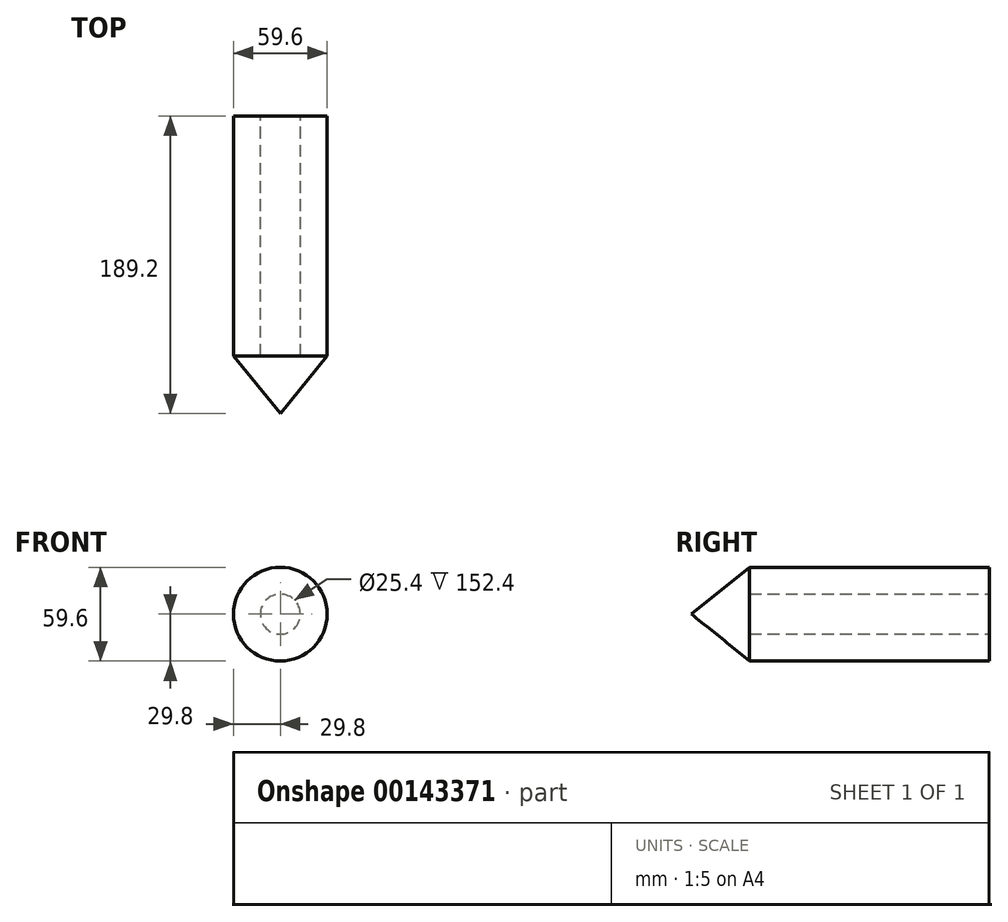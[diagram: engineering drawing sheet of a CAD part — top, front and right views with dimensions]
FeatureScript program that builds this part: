
annotation { "Feature Type Name" : "Feature", "Feature Type Description" : "" }
export const myFeature = defineFeature(function(context is Context, id is Id, definition is map)
    precondition{}
    {
        {
            var Q0;
            Q0=qCreatedBy(makeId("Front.planeOp"),FACE);
            var sketch = newSketch(context, id + "F0", { "sketchPlane" : qUnion([Q0])});
            skCircle(sketch, "E0", {"center": v(0, 0) * mm, "radius": 12.7 * mm});
            skCircle(sketch, "E1", {"center": v(0, 0) * mm, "radius": 29.8 * mm});
            skSolve(sketch);
        }
        {
            var Q0;
            Q0=makeQuery(id+"F0.imprint","IMPRINT",FACE,{"disambiguationData":[TD([[makeQuery(id+"F0.imprint","IMPRINT",EDGE,{"derivedFrom":sQuery(id+"F0.wireOp",EDGE,"E0")}),-1.0]])]});
            extrude(context, id + "F1", {"entities" : qUnion([Q0]), "depth" : 152.4 * mm});
        }
        {
            var Q0;
            Q0=makeQuery(id+"F1.opExtrude","CAP_FACE",FACE,{"disambiguationData":[OSD([sQuery(id+"F0.wireOp",EDGE,"E0"),sQuery(id+"F0.wireOp",EDGE,"E1")])],"isStart":false});
            var sketch = newSketch(context, id + "F2", { "sketchPlane" : qUnion([Q0])});
            skCircle(sketch, "E2.0", {"center": v(0, 0) * mm, "radius": 29.8 * mm});
            skSolve(sketch);
        }
        {
            var Q0;
            Q0 = qSketchRegion(id + "F2", true);
            extrude(context, id + "F3", {"entities" : qUnion([Q0]), "operationType" : NewBodyOperationType.ADD, "depth" : 50.8 * mm, "hasDraft" : true, "draftAngle" : 39 * degree, "draftPullDirection" : true});
        }
    });
